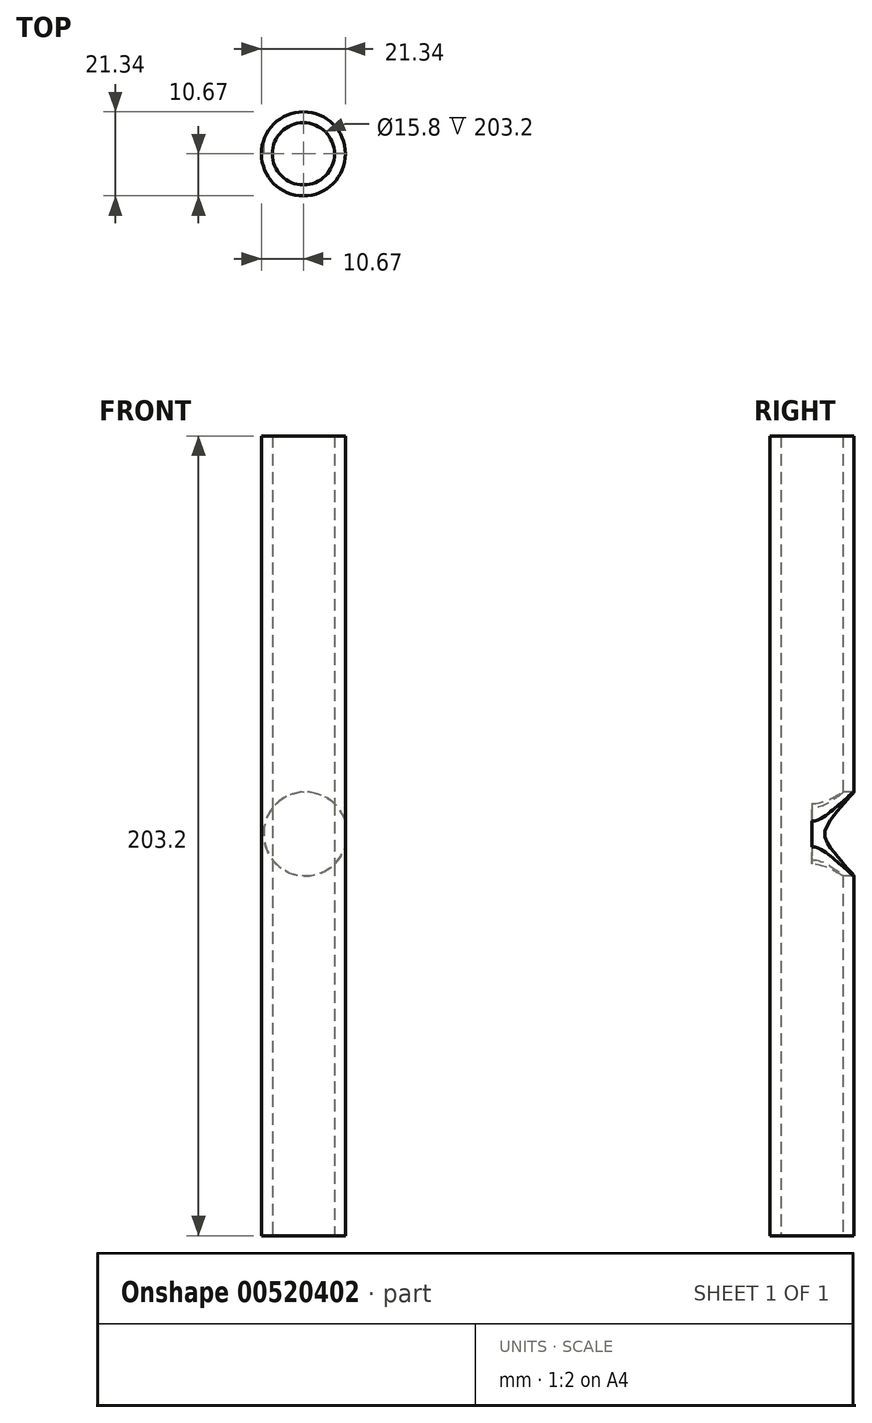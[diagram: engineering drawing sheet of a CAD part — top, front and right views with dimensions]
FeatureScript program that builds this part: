
annotation { "Feature Type Name" : "Feature", "Feature Type Description" : "" }
export const myFeature = defineFeature(function(context is Context, id is Id, definition is map)
    precondition{}
    {
        {
            var Q0;
            Q0=qCreatedBy(makeId("Top.planeOp"),FACE);
            var sketch = newSketch(context, id + "F0", { "sketchPlane" : qUnion([Q0])});
            skCircle(sketch, "E0", {"center": v(0, 0) * mm, "radius": 7.9 * mm});
            skCircle(sketch, "E1", {"center": v(0, 0) * mm, "radius": 1066.8 * mm});
            skCircle(sketch, "E2", {"center": v(0, 0) * mm, "radius": 10.67 * mm});
            skSolve(sketch);
        }
        {
            var Q0;
            Q0=makeQuery(id+"F0.imprint","IMPRINT",FACE,{"disambiguationData":[TD([[makeQuery(id+"F0.imprint","IMPRINT",EDGE,{"derivedFrom":sQuery(id+"F0.wireOp",EDGE,"E0")}),-1.0]])]});
            extrude(context, id + "F1", {"entities" : qUnion([Q0]), "depth" : 203.2 * mm, "offsetDistance" : 25.4 * mm});
        }
        {
            var Q0;
            Q0=qCreatedBy(makeId("Front.planeOp"),FACE);
            var sketch = newSketch(context, id + "F2", { "sketchPlane" : qUnion([Q0])});
            skCircle(sketch, "E3", {"center": v(0.51, 102.07) * mm, "radius": 7.9 * mm});
            skCircle(sketch, "E4", {"center": v(0.51, 102.07) * mm, "radius": 10.67 * mm});
            skSolve(sketch);
        }
        {
            var Q0;
            Q0=makeQuery(id+"F2.imprint","IMPRINT",FACE,{"disambiguationData":[TD([[makeQuery(id+"F2.imprint","IMPRINT",EDGE,{"derivedFrom":sQuery(id+"F2.wireOp",EDGE,"E3")}),1.0]])]});
            var Q1;
            Q1=makeQuery(id+"F2.imprint","IMPRINT",FACE,{"disambiguationData":[TD([[makeQuery(id+"F2.imprint","IMPRINT",EDGE,{"derivedFrom":sQuery(id+"F2.wireOp",EDGE,"E3")}),-1.0]])]});
            extrude(context, id + "F3", {"entities" : qUnion([Q0, Q1]), "operationType" : NewBodyOperationType.REMOVE, "oppositeDirection" : true, "depth" : 25.4 * mm, "offsetDistance" : 25.4 * mm});
        }
    });
